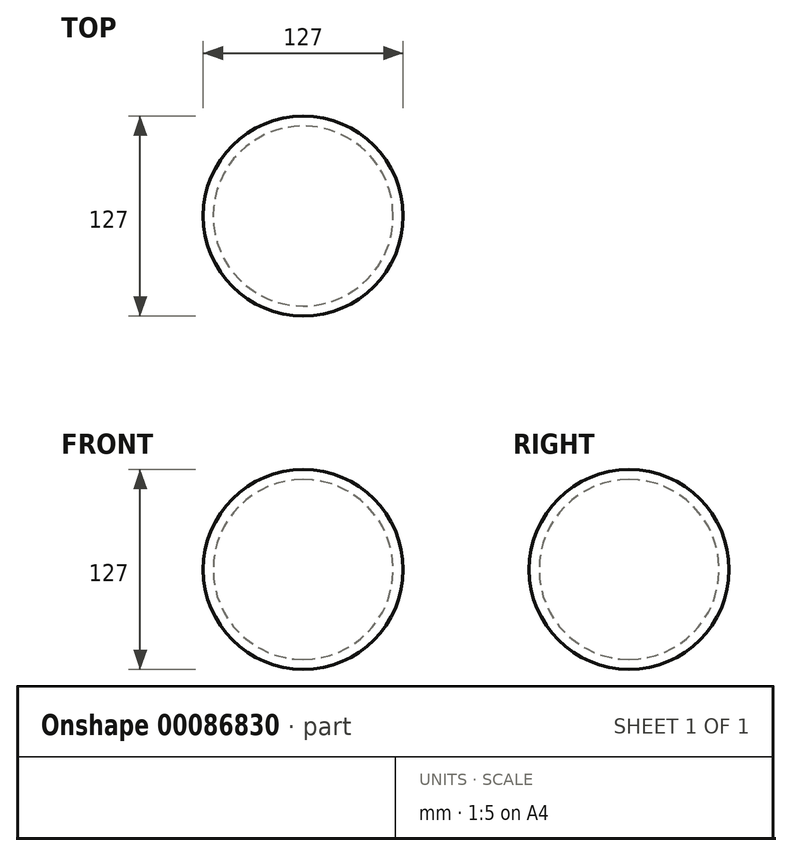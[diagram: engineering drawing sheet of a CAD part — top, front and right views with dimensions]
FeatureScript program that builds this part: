
annotation { "Feature Type Name" : "Feature", "Feature Type Description" : "" }
export const myFeature = defineFeature(function(context is Context, id is Id, definition is map)
    precondition{}
    {
        {
            var Q0;
            Q0=qCreatedBy(makeId("Front.planeOp"),FACE);
            var sketch = newSketch(context, id + "F0", { "sketchPlane" : qUnion([Q0])});
            skArc(sketch, "E0", {"start": v(0, -63.5) * mm, "mid": v(63.5, 0) * mm, "end": v(0, 63.5) * mm});
            skLineSegment(sketch, "E1", {"start": v(0, 63.5) * mm, "end": v(0, 57.15) * mm, "construction": true});
            skLineSegment(sketch, "E2", {"start": v(0, 63.5) * mm, "end": v(0, 57.15) * mm});
            skArc(sketch, "E3.0", {"start": v(0, -57.15) * mm, "mid": v(57.15, 0) * mm, "end": v(0, 57.15) * mm});
            skLineSegment(sketch, "E4.trimOffspring", {"start": v(0, -57.15) * mm, "end": v(0, -63.5) * mm});
            skLineSegment(sketch, "E5.trimOffspring", {"start": v(0, -57.15) * mm, "end": v(0, -63.5) * mm, "construction": true});
            skSolve(sketch);
        }
        {
            var Q0;
            Q0=qCreatedBy(makeId("Front.planeOp"),FACE);
            var sketch = newSketch(context, id + "F1", { "sketchPlane" : qUnion([Q0])});
            skLineSegment(sketch, "E6", {"start": v(0, 76.62) * mm, "end": v(0, -76.03) * mm, "construction": true});
            skSolve(sketch);
        }
        {
            var Q0;
            Q0 = qSketchRegion(id + "F1", true);
            var Q1;
            Q1=makeQuery(id+"F0.imprint","IMPRINT",FACE,{"disambiguationData":[TD([[makeQuery(id+"F0.imprint","IMPRINT",EDGE,{"derivedFrom":sQuery(id+"F0.wireOp",EDGE,"E0")}),1.0]])]});
            var Q2;
            Q2=sQuery(id+"F1.wireOp",EDGE,"E6");
            revolve(context, id + "F2", {"entities" : qUnion([Q0, Q1]), "axis" : qUnion([Q2]), "revolveType" : RevolveType.FULL});
        }
    });
